# Revit family: BUS11R
name_source: partatom
category: Electrical Fixtures
revit_build: Autodesk Revit 2018 (Build: 20170223_1515(x64)
units: mm (PartAtom-declared; Revit-internal decimal feet)

## family parameters
Always vertical = Yes
Cut with Voids When Loaded = No
Host = Ceiling
Maintain Annotation Orientation = No
Part Type = Normal
Room Calculation Point = No
Round Connector Dimension = Use Diameter
Shared = No

## types (5) — shared parameters
1A = Yes
2A = No
2D = No
3D = No
4B = No
4K = No
6A = No
6D = No
Busrun Length = 12' - 0"
Hanger Distance = 10' - 0"
Hangers = Yes

## per-type parameters (varying)
| type | MATERIAL | Support Height |
| BUS-11R1AXX1-12FEET-CP | CP-CUSTOM FINISH | 2' - 0" |
| BUS-11R1AXX1-12FEET-MB-BLACK | MB-BLACK | 1' - 0" |
| BUS-11R1AXX1-12FEET-NT BRUSHED ALUMINIUM | NT ALUMINIUM | 1' - 0" |
| BUS-11R1AXX1-12FEET-P WHITE | P WHITE | 1' - 0" |
| BUS-11R1AXX1-12FEET-UF | UF-UNFINISHED MILL | 1' - 0" |

## geometry (parser evidence)
native form markers: Blend x4, Sweep x15
no freeform markers — native parametric forms only
